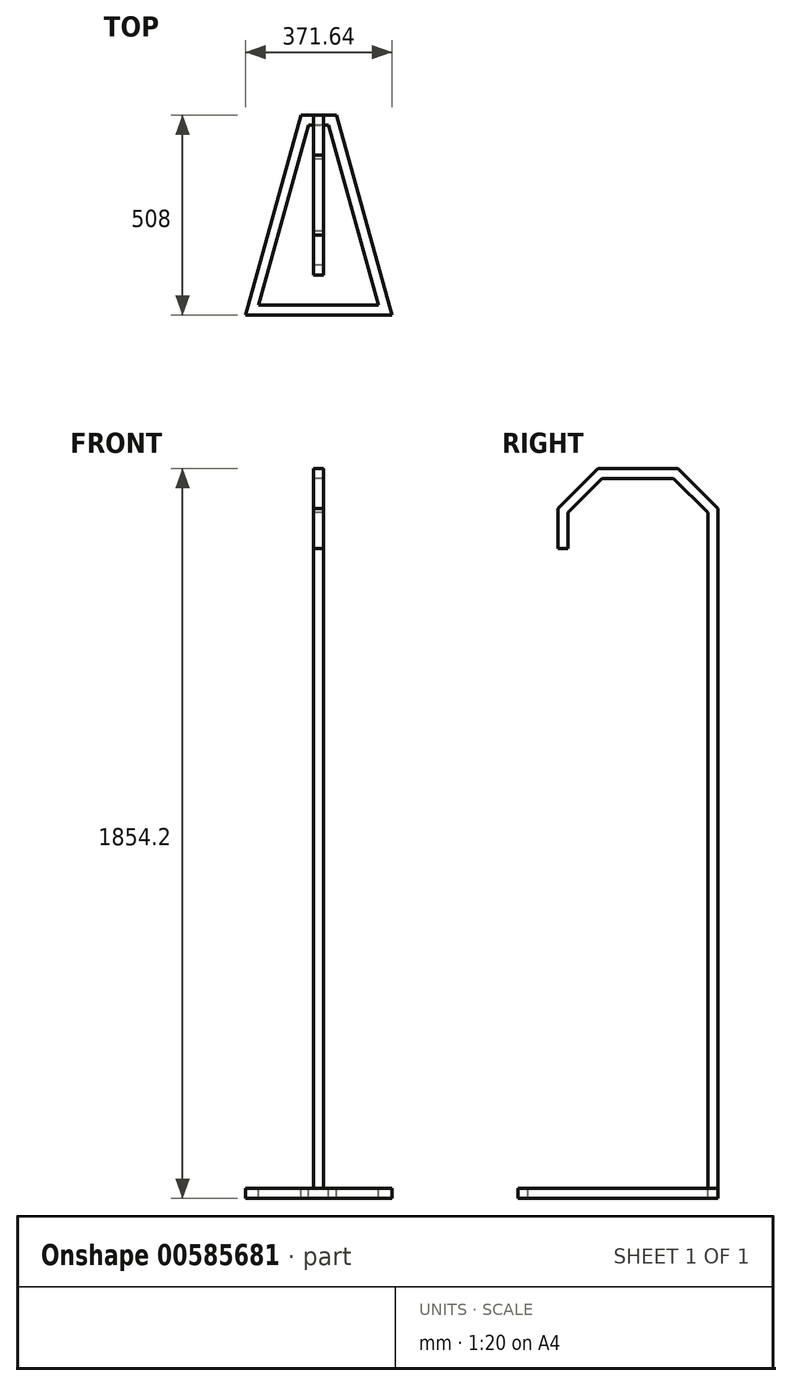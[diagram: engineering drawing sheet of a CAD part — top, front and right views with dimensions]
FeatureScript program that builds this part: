
annotation { "Feature Type Name" : "Feature", "Feature Type Description" : "" }
export const myFeature = defineFeature(function(context is Context, id is Id, definition is map)
    precondition{}
    {
        {
            var Q0;
            Q0=qCreatedBy(makeId("Top.planeOp"),FACE);
            var sketch = newSketch(context, id + "F0", { "sketchPlane" : qUnion([Q0])});
            skLineSegment(sketch, "E0", {"start": v(-44.7, 508) * mm, "end": v(44.7, 508) * mm});
            skLineSegment(sketch, "E1", {"start": v(44.7, 508) * mm, "end": v(185.82, 0) * mm});
            skLineSegment(sketch, "E2", {"start": v(185.82, 0) * mm, "end": v(-185.82, 0) * mm});
            skLineSegment(sketch, "E3", {"start": v(-185.82, 0) * mm, "end": v(-44.7, 508) * mm});
            skLineSegment(sketch, "E4", {"start": v(-25.4, 482.6) * mm, "end": v(25.4, 482.6) * mm});
            skLineSegment(sketch, "E5", {"start": v(25.4, 482.6) * mm, "end": v(152.4, 25.4) * mm});
            skLineSegment(sketch, "E6", {"start": v(152.4, 25.4) * mm, "end": v(-152.4, 25.4) * mm});
            skLineSegment(sketch, "E7", {"start": v(-152.4, 25.4) * mm, "end": v(-25.4, 482.6) * mm});
            skSolve(sketch);
        }
        {
            var Q0;
            Q0=makeQuery(id+"F0.imprint","IMPRINT",FACE,{"disambiguationData":[TD([[makeQuery(id+"F0.imprint","IMPRINT",EDGE,{"derivedFrom":sQuery(id+"F0.wireOp",EDGE,"E0")}),-1.0]])]});
            extrude(context, id + "F1", {"entities" : qUnion([Q0]), "oppositeDirection" : true, "depth" : 25.4 * mm, "offsetDistance" : 25.4 * mm});
        }
        {
            var Q0;
            Q0=qCreatedBy(makeId("Top.planeOp"),FACE);
            var sketch = newSketch(context, id + "F2", { "sketchPlane" : qUnion([Q0])});
            skLineSegment(sketch, "E8.bottom", {"start": v(-12.7, 508) * mm, "end": v(12.7, 508) * mm});
            skLineSegment(sketch, "E8.top", {"start": v(-12.7, 482.6) * mm, "end": v(12.7, 482.6) * mm});
            skLineSegment(sketch, "E8.left", {"start": v(-12.7, 508) * mm, "end": v(-12.7, 482.6) * mm});
            skLineSegment(sketch, "E8.right", {"start": v(12.7, 508) * mm, "end": v(12.7, 482.6) * mm});
            skSolve(sketch);
        }
        {
            var Q0;
            Q0=qCreatedBy(makeId("Right.planeOp"),FACE);
            var sketch = newSketch(context, id + "F3", { "sketchPlane" : qUnion([Q0])});
            skLineSegment(sketch, "E9", {"start": v(508, 0) * mm, "end": v(508, 1727.2) * mm});
            skLineSegment(sketch, "E10", {"start": v(508, 1727.2) * mm, "end": v(406.4, 1828.8) * mm});
            skLineSegment(sketch, "E11", {"start": v(406.4, 1828.8) * mm, "end": v(203.2, 1828.8) * mm});
            skLineSegment(sketch, "E12", {"start": v(203.2, 1828.8) * mm, "end": v(101.6, 1727.2) * mm});
            skLineSegment(sketch, "E13", {"start": v(101.6, 1727.2) * mm, "end": v(101.6, 1625.6) * mm});
            skSolve(sketch);
        }
        {
            var Q0;
            Q0=makeQuery(id+"F2.imprint","IMPRINT",FACE,{"disambiguationData":[TD([[makeQuery(id+"F2.imprint","IMPRINT",EDGE,{"derivedFrom":sQuery(id+"F2.wireOp",EDGE,"E8.bottom")}),-1.0]])]});
            var Q1;
            Q1=sQuery(id+"F3.wireOp",EDGE,"E9");
            var Q2;
            Q2=sQuery(id+"F3.wireOp",EDGE,"E13");
            var Q3;
            Q3=sQuery(id+"F3.wireOp",EDGE,"E12");
            var Q4;
            Q4=sQuery(id+"F3.wireOp",EDGE,"E11");
            var Q5;
            Q5=sQuery(id+"F3.wireOp",EDGE,"E10");
            sweep(context, id + "F4", {"operationType" : NewBodyOperationType.ADD, "profiles" : qUnion([Q0]), "path" : qUnion([Q1, Q2, Q3, Q4, Q5])});
        }
    });
